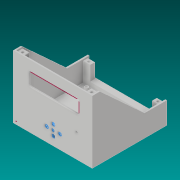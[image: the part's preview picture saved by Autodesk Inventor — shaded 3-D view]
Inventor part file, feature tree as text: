
AUTODESK INVENTOR PART (.ipt)
format: ipt  version: 2019 (Build 230136000, 136)  size: 1,330,688 bytes
history: native  units: mm
features: sketch x64, extrude x39, other x12, delete_face x12, fillet x11, hole x8, boolean_combine x3
ambient origin geometry x8: Origin, YZ Plane, XZ Plane, XY Plane, X Axis, Y Axis, Z Axis, Center Point
bodies: Solid1 (feature_tree), Solid2 (feature_tree), Solid3 (feature_tree), Solid4 (feature_tree), Solid5 (feature_tree), Solid6 (feature_tree), Solid137 (feature_tree), Solid139 (feature_tree), Solid141 (feature_tree), Solid142 (feature_tree), Solid143 (feature_tree), Solid144 (feature_tree), Solid145 (feature_tree), Solid146 (feature_tree)
feature tree (149):
  other  "Repaired Geometry1"
  other  "Repaired Geometry2"
  extrude  "Extrusion1"  Depth=2.0mm TaperAngle=0.0deg
  sketch  "Sketch2"  dims[d5=4.5mm d6=5.0mm d7=0.0mm]
  extrude  "Extrusion2"  Depth=5.0mm TaperAngle=0.0deg
  extrude  "Extrusion3"  Depth=5.0mm TaperAngle=0.0deg
  extrude  "Extrusion4"  Depth=5.0mm TaperAngle=0.0deg
  extrude  "Extrusion5"  Depth=5.0mm TaperAngle=0.0deg
  extrude  "Extrusion6"  Depth=5.0mm TaperAngle=0.0deg
  extrude  "Extrusion7"  Depth=5.0mm TaperAngle=0.0deg
  sketch  "Sketch10"  dims[d31=2.0mm d32=2.0mm d33=0.0mm d34=2.0mm]
  sketch  "Sketch11"  dims[d35=2.0mm d36=0.0mm d37=2.0mm]
  extrude  "Extrusion8"  Depth=20.0mm TaperAngle=0.0deg
  extrude  "Extrusion9"  Depth=2.0mm TaperAngle=0.0deg
  boolean_combine  "Combine1"
  boolean_combine  "Combine2"
  boolean_combine  "Combine3"
  delete_face  "Delete Face1"
  delete_face  "Delete Face2"
  extrude  "Extrusion10"  Depth=2.0mm TaperAngle=0.0deg
  fillet  "Fillet1"  Radius=2.0mm
  extrude  "Extrusion11"  Depth=2.0mm
  fillet  "Fillet2"  Radius=3.0mm
  extrude  "Extrusion12"  Depth=2.0mm
  fillet  "Fillet3"  Radius=0.5mm
  sketch  "Sketch16"  dims[d60=2.0mm d61=0.0mm d62=10.0mm]
  sketch  "Sketch17"  dims[d63=10.0mm d64=10.0mm]
  extrude  "Extrusion13"  Depth=2.0mm TaperAngle=0.0deg
  fillet  "Fillet4"  Radius=2.0mm
  fillet  "Fillet5"  Radius=4.5mm
  fillet  "Fillet6"  Radius=4.5mm
  fillet  "Fillet7"  Radius=2.0mm
  fillet  "Fillet8"  Radius=4.5mm
  extrude  "Extrusion14"  Depth=2.0mm
  sketch  "Sketch20"  dims[d70=2.0mm d71=0.0mm d72=1.0mm]
  extrude  "Extrusion15"  Depth=10.0mm
  extrude  "Extrusion16"  Depth=10.0mm
  extrude  "Extrusion17"  Depth=10.0mm TaperAngle=0.0deg
  extrude  "Extrusion18"  Depth=2.0mm
  extrude  "Extrusion19"  Depth=1.0mm
  fillet  "Fillet9"  Radius=8.5mm
  extrude  "Extrusion20"  Depth=2.0mm TaperAngle=0.0deg
  fillet  "Fillet10"  Radius=2.0mm
  sketch  "Sketch27"  dims[d109=2.1mm d110=0.0mm d111=9.5mm]
  hole  "Hole1"  [1 undecoded]
  hole  "Hole2"  [1 undecoded]
  hole  "Hole3"  [1 undecoded]
  other  "Solid9:2"
  sketch  "3D Sketch2"
  sketch  "3D Sketch3"
  sketch  "3D Sketch4"
  sketch  "3D Sketch5"
  sketch  "3D Sketch6"
  extrude  "Extrusion21"  Depth=2.1mm TaperAngle=0.0deg
  extrude  "Extrusion22"  Depth=8.5mm
  extrude  "Extrusion23"  Depth=2.1mm TaperAngle=0.0deg
  sketch  "Sketch34"  dims[d129=2.0mm d130=0.0mm d131=9.5mm]
  sketch  "Sketch35"  dims[d132=8.5mm]
  extrude  "Extrusion24"  Depth=8.5mm
  extrude  "Extrusion25"  Depth=9.5mm
  extrude  "Extrusion26"  Depth=2.1mm TaperAngle=0.0deg
  extrude  "Extrusion27"  Depth=9.5mm
  extrude  "Extrusion28"  Depth=9.5mm
  extrude  "Extrusion29"  Depth=20.0mm
  extrude  "Extrusion30"  Depth=2.0mm TaperAngle=0.0deg
  extrude  "Extrusion31"  Depth=2.0mm
  hole  "Hole4"  [1 undecoded]
  hole  "Hole5"  [1 undecoded]
  extrude  "Extrusion32"  Depth=9.5mm
  extrude  "Extrusion33"  Depth=2.0mm TaperAngle=0.0deg
  extrude  "Extrusion34"  Depth=9.5mm
  extrude  "Extrusion35"  Depth=2.1mm TaperAngle=0.0deg
  fillet  "Fillet11"  Radius=2.1mm
  extrude  "Extrusion36"  Depth=1.0mm
  extrude  "Extrusion37"  [1 undecoded]
  hole  "Hole6"  [1 undecoded]
  extrude  "Extrusion38"  [1 undecoded]
  extrude  "Extrusion39"  [1 undecoded]
  hole  "Hole7"  [1 undecoded]
  sketch  "Sketch55"
  sketch  "Sketch56"
  sketch  "Sketch57"
  hole  "Hole8"  [1 undecoded]
  sketch  "Sketch59"
  delete_face  "Delete Face3"
  delete_face  "Delete Face4"
  delete_face  "Delete Face9"
  delete_face  "Delete Face10"
  delete_face  "Delete Face11"
  delete_face  "Delete Face12"
  delete_face  "Delete Face13"
  delete_face  "Delete Face14"
  delete_face  "Delete Face18"
  delete_face  "Delete Face22"
  sketch  "Sketch8"  dims[d24=3.0mm d25=20.0mm d26=0.0mm]
  sketch  "Sketch1"  dims[d1=1.0mm d2=2.0mm d3=0.0mm]
  sketch  "Sketch3"  dims[d8=4.5mm d9=5.0mm d10=0.0mm]
  sketch  "Sketch4"  dims[d11=4.5mm d12=5.0mm d13=0.0mm]
  sketch  "Sketch5"  dims[d14=4.5mm d15=5.0mm d16=0.0mm]
  sketch  "Sketch6"  dims[d17=4.5mm d18=5.0mm d19=0.0mm]
  sketch  "Sketch7"  dims[d20=4.5mm d21=5.0mm d22=0.0mm]
  sketch  "Sketch9"  dims[d27=2.0mm d28=0.0mm d29=2.0mm d30=0.0mm]
  sketch  "Sketch12"  dims[d39=100.0mm d40=2.0mm d41=0.0mm d42=0.0mm d43=3.0mm]
  sketch  "Sketch13"  dims[d44=2.0mm d45=0.5mm d46=0.5mm]
  sketch  "Sketch14"  dims[d47=1.0mm d48=2.0mm d49=0.0mm d50=2.0mm d51=0.0mm d52=4.5mm d53=4.5mm d54=2.0mm d55=0.0mm d56=4.5mm]
  sketch  "Sketch15"  dims[d57=2.0mm d58=0.0mm d59=4.5mm]
  sketch  "Sketch18"  dims[d65=10.0mm d66=5.0mm d67=0.0mm]
  sketch  "Sketch19"  dims[d68=1.0mm d69=2.0mm]
  sketch  "Sketch21"  dims[d73=3.2mm d74=6.0mm d75=4.0mm d76=2.0mm d77=90.0deg d78=4.0mm d79=0.0mm]
  sketch  "Sketch22"  dims[d80=3.2mm d81=6.0mm d82=4.0mm d83=2.0mm d84=90.0deg d85=4.0mm d86=0.0mm]
  sketch  "Sketch23"  dims[d87=3.2mm d88=6.0mm d89=4.0mm d90=2.0mm d91=90.0deg d92=4.0mm d93=0.0mm d94=8.5mm]
  sketch  "Sketch24"  dims[d96=2.0mm d97=0.0mm d98=2.0mm d99=0.0mm d100=2.0mm d101=0.0mm]
  sketch  "Sketch25"  dims[d104=9.5mm d105=8.0mm d106=0.0mm]
  sketch  "Sketch26"  dims[d107=9.5mm d108=8.5mm]
  sketch  "Sketch28"  dims[d112=8.5mm d113=2.1mm d114=0.0mm]
  sketch  "Sketch29"  dims[d115=9.5mm d116=8.5mm]
  sketch  "Sketch30"  dims[d117=2.1mm d118=0.0mm d119=2.1mm d120=0.0mm]
  sketch  "3D Sketch7"
  sketch  "Sketch31"  dims[d121=9.5mm d122=8.5mm]
  sketch  "Sketch32"  dims[d123=2.1mm d124=0.0mm d125=9.5mm]
  sketch  "Sketch33"  dims[d126=8.5mm d127=2.1mm d128=0.0mm]
  sketch  "Sketch36"  dims[d133=3.2mm d134=6.0mm d135=4.0mm d136=2.0mm d137=90.0deg d138=4.0mm d139=0.0mm d140=9.5mm]
  sketch  "Sketch37"  dims[d141=8.5mm]
  sketch  "Sketch38"  dims[d142=3.2mm d143=6.0mm d144=4.0mm d145=2.0mm d146=90.0deg d147=4.0mm d148=0.0mm d149=20.0mm]
  sketch  "Sketch39"  dims[d150=2.0mm d151=0.0mm d152=2.0mm d153=0.0mm]
  sketch  "Sketch40"  dims[d154=2.0mm d155=0.0mm d157=5.0mm]
  sketch  "Sketch41"  dims[d159=5.0mm d161=5.0mm]
  sketch  "Sketch42"  dims[d163=5.0mm d164=2.0mm d165=0.0mm]
  sketch  "Sketch44"  dims[d166=1.0mm d167=9.5mm]
  sketch  "Sketch45"  dims[d168=6.5mm d169=2.0mm d170=0.0mm]
  sketch  "Sketch46"  dims[d171=2.1mm d172=0.0mm]
  sketch  "Sketch47"  dims[d173=3.2mm d174=6.0mm d175=4.0mm d176=2.0mm d177=90.0deg d178=4.0mm d179=0.0mm d180=9.5mm]
  sketch  "Sketch48"  dims[d181=6.5mm d182=2.1mm d183=0.0mm d184=2.1mm d185=0.0mm]
  sketch  "Sketch49"  dims[d186=3.2mm d187=6.0mm d188=4.0mm d189=2.0mm d190=90.0deg d191=4.0mm d192=0.0mm]
  sketch  "Sketch50"  dims[d193=3.2mm d194=6.0mm d195=4.0mm d196=2.0mm d197=90.0deg d198=4.0mm d199=0.0mm d38=1.0mm]
  sketch  "Sketch51"
  sketch  "Sketch52"
  sketch  "Sketch53"
  sketch  "Sketch54"
  sketch  "Sketch58"
  other  "Open CASCADE STEP translator 6.8 1.1.1_1:1"
  other  "4301x60507x6_3:1"
  other  "4301x60507x6_5:1"
  other  "4301x60507x6_7:1"
  other  "4301x60507x6_9:1"
  other  "4301x60507x6_11:1"
  other  "RC1602B-BIW-CSV--3DModel-STEP-56544_70:28"
  other  "RC1602B-BIW-CSV--3DModel-STEP-56544_70:30"
  other  "Solid9:1"
note: 11 required parameter values undecoded (feature->parameter linkage not recoverable at this tier; creation-order binding heuristic only, values carry confidence <= 0.55)
